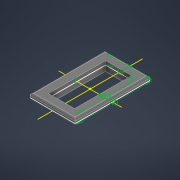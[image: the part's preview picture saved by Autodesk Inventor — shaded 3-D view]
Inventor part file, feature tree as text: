
AUTODESK INVENTOR PART (.ipt)
format: ipt  version: 2022 (Build 260153000, 153)  size: 259,072 bytes
history: native  units: mm
features: extrude x2, sketch x1, fillet x1
ambient origin geometry x8: Origin, YZ Plane, XZ Plane, XY Plane, X Axis, Y Axis, Z Axis, Center Point
bodies: Solid1 (feature_tree)
feature tree (4):
  sketch  "Sketch1"  dims[d0=14.0mm d1=30.5mm d2=2.0mm d3=24.0mm d4=40.0mm d5=3.0mm d6=0.0mm d7=2.0mm d8=0.0mm d9=1.0mm]
  extrude  "Extrusion1"  Depth=30.5mm
  extrude  "Extrusion2"  Depth=2.0mm
  fillet  "Fillet1"  Radius=24.0mm
